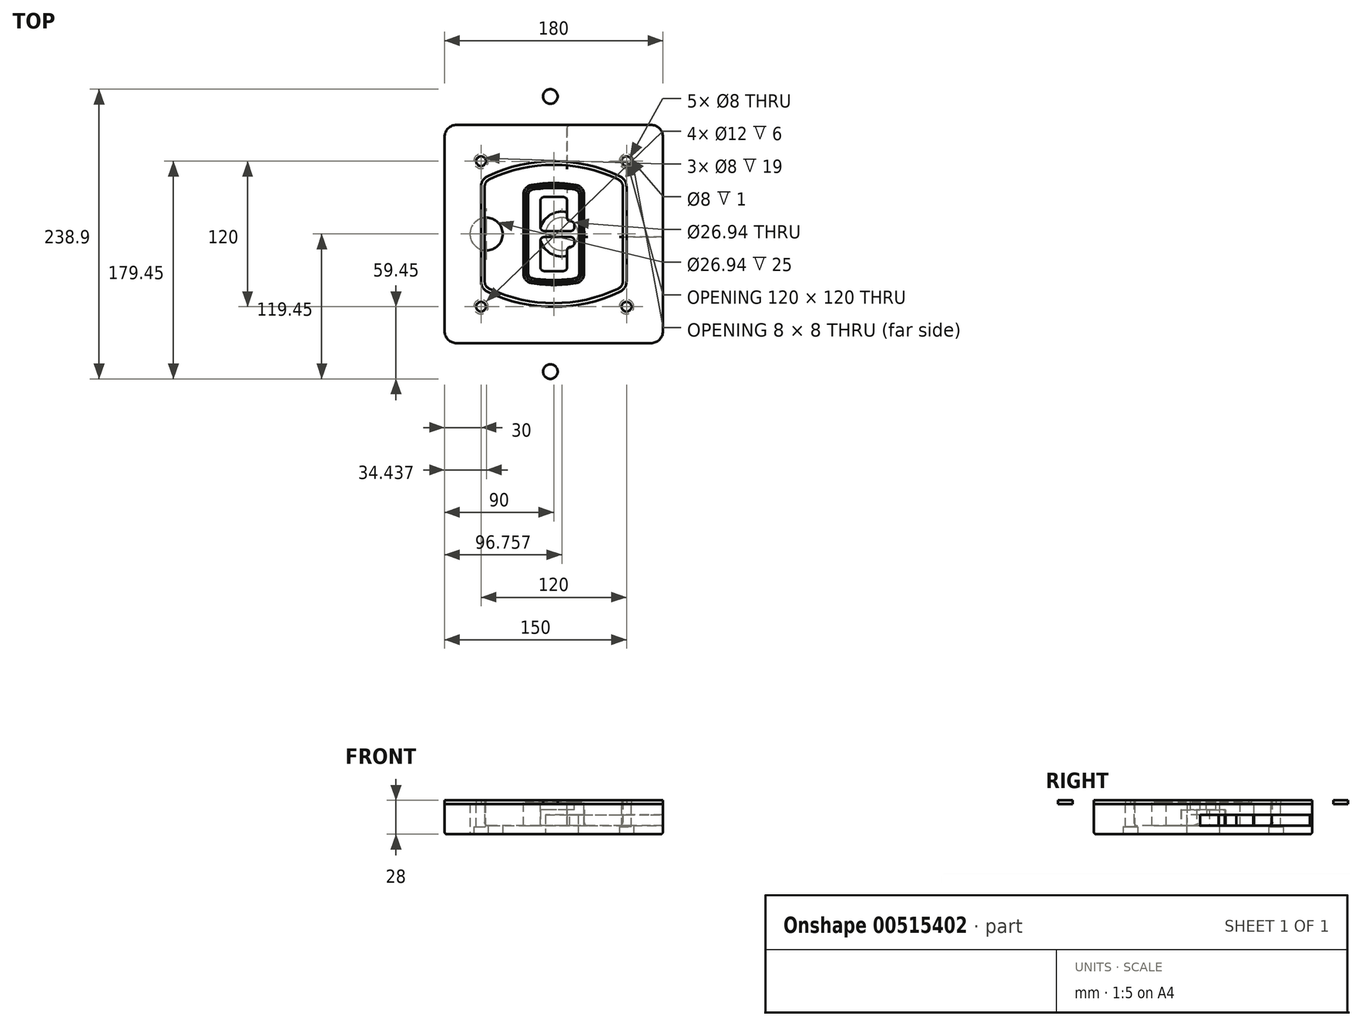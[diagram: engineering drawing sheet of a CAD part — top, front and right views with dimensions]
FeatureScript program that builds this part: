
annotation { "Feature Type Name" : "Feature", "Feature Type Description" : "" }
export const myFeature = defineFeature(function(context is Context, id is Id, definition is map)
    precondition{}
    {
        {
            var Q0;
            Q0=qCreatedBy(makeId("Top.planeOp"),FACE);
            var sketch = newSketch(context, id + "F0", { "sketchPlane" : qUnion([Q0])});
            skPoint(sketch, "E0.rect.middle", {"position": v(0, 0) * mm});
            skLineSegment(sketch, "E1.bottom", {"start": v(-80, -90) * mm, "end": v(80, -90) * mm});
            skLineSegment(sketch, "E1.top", {"start": v(-80, 90) * mm, "end": v(80, 90) * mm});
            skLineSegment(sketch, "E1.left", {"start": v(-90, -80) * mm, "end": v(-90, 80) * mm});
            skLineSegment(sketch, "E1.right", {"start": v(90, -80) * mm, "end": v(90, 80) * mm});
            skLineSegment(sketch, "E2", {"start": v(-90, 90) * mm, "end": v(90, -90) * mm, "construction": true});
            skLineSegment(sketch, "E3", {"start": v(90, 90) * mm, "end": v(-90, -90) * mm, "construction": true});
            skCircle(sketch, "E4", {"center": v(-60, 60) * mm, "radius": 4 * mm});
            skCircle(sketch, "E5", {"center": v(60, 60) * mm, "radius": 4 * mm});
            skCircle(sketch, "E6", {"center": v(60, -60) * mm, "radius": 4 * mm});
            skCircle(sketch, "E7", {"center": v(-60, -60) * mm, "radius": 4 * mm});
            skLineSegment(sketch, "E8", {"start": v(-60, 60) * mm, "end": v(60, 60) * mm, "construction": true});
            skLineSegment(sketch, "E9", {"start": v(60, 60) * mm, "end": v(60, -60) * mm, "construction": true});
            skLineSegment(sketch, "E10", {"start": v(60, -60) * mm, "end": v(-60, -60) * mm, "construction": true});
            skLineSegment(sketch, "E11", {"start": v(-60, -60) * mm, "end": v(-60, 60) * mm, "construction": true});
            skLineSegment(sketch, "E12", {"start": v(-60, 38.83) * mm, "end": v(-60, -38.83) * mm});
            skLineSegment(sketch, "E13", {"start": v(60, 38.83) * mm, "end": v(60, -38.83) * mm});
            skArc(sketch, "E14", {"start": v(54.26, 47.88) * mm, "mid": v(0, 60) * mm, "end": v(-54.26, 47.88) * mm});
            skArc(sketch, "E15", {"start": v(-54.26, -47.88) * mm, "mid": v(0, -60) * mm, "end": v(54.26, -47.88) * mm});
            skLineSegment(sketch, "E16", {"start": v(-60, 0) * mm, "end": v(60, 0) * mm, "construction": true});
            skPoint(sketch, "E17.visualSharp", {"position": v(-60, -45) * mm});
            skArc(sketch, "E17.filletArc", {"start": v(-60, -38.83) * mm, "mid": v(-58.44, -44.2) * mm, "end": v(-54.26, -47.88) * mm});
            skPoint(sketch, "E18.visualSharp", {"position": v(-60, 45) * mm});
            skArc(sketch, "E18.filletArc", {"start": v(-54.26, 47.88) * mm, "mid": v(-58.44, 44.2) * mm, "end": v(-60, 38.83) * mm});
            skPoint(sketch, "E19.visualSharp", {"position": v(60, 45) * mm});
            skArc(sketch, "E19.filletArc", {"start": v(60, 38.83) * mm, "mid": v(58.44, 44.2) * mm, "end": v(54.26, 47.88) * mm});
            skPoint(sketch, "E20.visualSharp", {"position": v(60, -45) * mm});
            skArc(sketch, "E20.filletArc", {"start": v(54.26, -47.88) * mm, "mid": v(58.44, -44.2) * mm, "end": v(60, -38.83) * mm});
            skPoint(sketch, "E21.visualSharp", {"position": v(-90, 90) * mm});
            skArc(sketch, "E21.filletArc", {"start": v(-80, 90) * mm, "mid": v(-87.07, 87.07) * mm, "end": v(-90, 80) * mm});
            skPoint(sketch, "E22.visualSharp", {"position": v(90, 90) * mm});
            skArc(sketch, "E22.filletArc", {"start": v(90, 80) * mm, "mid": v(87.07, 87.07) * mm, "end": v(80, 90) * mm});
            skPoint(sketch, "E23.visualSharp", {"position": v(90, -90) * mm});
            skArc(sketch, "E23.filletArc", {"start": v(80, -90) * mm, "mid": v(87.07, -87.07) * mm, "end": v(90, -80) * mm});
            skPoint(sketch, "E24.visualSharp", {"position": v(-90, -90) * mm});
            skArc(sketch, "E24.filletArc", {"start": v(-90, -80) * mm, "mid": v(-87.07, -87.07) * mm, "end": v(-80, -90) * mm});
            skArc(sketch, "E25.0", {"start": v(57, 38.83) * mm, "mid": v(55.9, 42.58) * mm, "end": v(52.98, 45.17) * mm});
            skLineSegment(sketch, "E25.1", {"start": v(57, 38.83) * mm, "end": v(57, -38.83) * mm});
            skArc(sketch, "E25.2", {"start": v(52.98, -45.17) * mm, "mid": v(55.9, -42.58) * mm, "end": v(57, -38.83) * mm});
            skArc(sketch, "E25.3", {"start": v(-52.98, -45.17) * mm, "mid": v(0, -57) * mm, "end": v(52.98, -45.17) * mm});
            skArc(sketch, "E25.4", {"start": v(-57, -38.83) * mm, "mid": v(-55.9, -42.58) * mm, "end": v(-52.98, -45.17) * mm});
            skArc(sketch, "E25.5", {"start": v(52.98, 45.17) * mm, "mid": v(0, 57) * mm, "end": v(-52.98, 45.17) * mm});
            skLineSegment(sketch, "E25.6", {"start": v(-57, 38.83) * mm, "end": v(-57, -38.83) * mm});
            skArc(sketch, "E25.7", {"start": v(-52.98, 45.17) * mm, "mid": v(-55.9, 42.58) * mm, "end": v(-57, 38.83) * mm});
            skArc(sketch, "E26.0", {"start": v(-55.96, 51.5) * mm, "mid": v(-61.82, 46.33) * mm, "end": v(-64, 38.83) * mm});
            skArc(sketch, "E26.1", {"start": v(55.96, 51.5) * mm, "mid": v(0, 64) * mm, "end": v(-55.96, 51.5) * mm});
            skArc(sketch, "E26.2", {"start": v(64, 38.83) * mm, "mid": v(61.82, 46.33) * mm, "end": v(55.96, 51.5) * mm});
            skLineSegment(sketch, "E26.3", {"start": v(64, 38.83) * mm, "end": v(64, -38.83) * mm});
            skArc(sketch, "E26.4", {"start": v(55.96, -51.5) * mm, "mid": v(61.82, -46.33) * mm, "end": v(64, -38.83) * mm});
            skLineSegment(sketch, "E26.5", {"start": v(-64, 38.83) * mm, "end": v(-64, -38.83) * mm});
            skArc(sketch, "E26.6", {"start": v(-55.96, -51.5) * mm, "mid": v(0, -64) * mm, "end": v(55.96, -51.5) * mm});
            skArc(sketch, "E26.7", {"start": v(-64, -38.83) * mm, "mid": v(-61.82, -46.33) * mm, "end": v(-55.96, -51.5) * mm});
            skSolve(sketch);
        }
        {
            var Q0;
            Q0=makeQuery(id+"F0.imprint","IMPRINT",FACE,{"disambiguationData":[TD([[makeQuery(id+"F0.imprint","IMPRINT",EDGE,{"derivedFrom":sQuery(id+"F0.wireOp",EDGE,"E1.bottom")}),1.0]])]});
            var Q1;
            Q1=makeQuery(id+"F0.imprint","IMPRINT",FACE,{"disambiguationData":[TD([[makeQuery(id+"F0.imprint","IMPRINT",EDGE,{"derivedFrom":sQuery(id+"F0.wireOp",EDGE,"E12")}),1.0]])]});
            var Q2;
            Q2=makeQuery(id+"F0.imprint","IMPRINT",FACE,{"disambiguationData":[TD([[makeQuery(id+"F0.imprint","IMPRINT",EDGE,{"derivedFrom":sQuery(id+"F0.wireOp",EDGE,"E25.0")}),1.0]])]});
            var Q3;
            Q3=makeQuery(id+"F0.imprint","IMPRINT",FACE,{"disambiguationData":[TD([[makeQuery(id+"F0.imprint","IMPRINT",EDGE,{"derivedFrom":sQuery(id+"F0.wireOp",EDGE,"E12")}),-1.0]])]});
            extrude(context, id + "F1", {"entities" : qUnion([Q0, Q1, Q2, Q3]), "oppositeDirection" : true, "depth" : 25 * mm});
        }
        {
            var Q0;
            Q0=makeQuery(id+"F0.imprint","IMPRINT",FACE,{"disambiguationData":[TD([[makeQuery(id+"F0.imprint","IMPRINT",EDGE,{"derivedFrom":sQuery(id+"F0.wireOp",EDGE,"E12")}),1.0]])]});
            extrude(context, id + "F2", {"entities" : qUnion([Q0]), "operationType" : NewBodyOperationType.ADD, "depth" : 3 * mm});
        }
        {
            var Q0;
            Q0=makeQuery(id+"F0.imprint","IMPRINT",FACE,{"disambiguationData":[TD([[makeQuery(id+"F0.imprint","IMPRINT",EDGE,{"derivedFrom":sQuery(id+"F0.wireOp",EDGE,"E25.0")}),1.0]])]});
            extrude(context, id + "F3", {"entities" : qUnion([Q0]), "operationType" : NewBodyOperationType.REMOVE, "oppositeDirection" : true, "depth" : 18 * mm});
        }
        {
            var Q0;
            Q0=makeQuery(id+"F2.opExtrude","CAP_FACE",FACE,{"disambiguationData":[OSD([sQuery(id+"F0.wireOp",EDGE,"E12"),sQuery(id+"F0.wireOp",EDGE,"E13"),sQuery(id+"F0.wireOp",EDGE,"E14"),sQuery(id+"F0.wireOp",EDGE,"E15"),sQuery(id+"F0.wireOp",EDGE,"E17.filletArc"),sQuery(id+"F0.wireOp",EDGE,"E18.filletArc"),sQuery(id+"F0.wireOp",EDGE,"E19.filletArc"),sQuery(id+"F0.wireOp",EDGE,"E20.filletArc"),sQuery(id+"F0.wireOp",EDGE,"E25.0"),sQuery(id+"F0.wireOp",EDGE,"E25.1"),sQuery(id+"F0.wireOp",EDGE,"E25.2"),sQuery(id+"F0.wireOp",EDGE,"E25.3"),sQuery(id+"F0.wireOp",EDGE,"E25.4"),sQuery(id+"F0.wireOp",EDGE,"E25.5"),sQuery(id+"F0.wireOp",EDGE,"E25.6"),sQuery(id+"F0.wireOp",EDGE,"E25.7")])],"isStart":false});
            var sketch = newSketch(context, id + "F4", { "sketchPlane" : qUnion([Q0])});
            skArc(sketch, "E27.0", {"start": v(-18.34, -40.45) * mm, "mid": v(0, -42) * mm, "end": v(18.34, -40.45) * mm});
            skArc(sketch, "E28.0", {"start": v(18.34, 40.45) * mm, "mid": v(0, 42) * mm, "end": v(-18.34, 40.45) * mm});
            skLineSegment(sketch, "E29", {"start": v(-25, 32.57) * mm, "end": v(-25, -32.57) * mm});
            skLineSegment(sketch, "E30", {"start": v(25, 32.57) * mm, "end": v(25, -32.57) * mm});
            skLineSegment(sketch, "E31", {"start": v(-25, 39.1) * mm, "end": v(25, 39.1) * mm, "construction": true});
            skLineSegment(sketch, "E32", {"start": v(-25, -39.1) * mm, "end": v(25, -39.1) * mm, "construction": true});
            skPoint(sketch, "E33.visualSharp", {"position": v(-25, 39.1) * mm});
            skArc(sketch, "E33.filletArc", {"start": v(-18.34, 40.45) * mm, "mid": v(-23.11, 37.73) * mm, "end": v(-25, 32.57) * mm});
            skPoint(sketch, "E34.visualSharp", {"position": v(25, 39.1) * mm});
            skArc(sketch, "E34.filletArc", {"start": v(25, 32.57) * mm, "mid": v(23.11, 37.73) * mm, "end": v(18.34, 40.45) * mm});
            skPoint(sketch, "E35.visualSharp", {"position": v(25, -39.1) * mm});
            skArc(sketch, "E35.filletArc", {"start": v(18.34, -40.45) * mm, "mid": v(23.11, -37.73) * mm, "end": v(25, -32.57) * mm});
            skPoint(sketch, "E36.visualSharp", {"position": v(-25, -39.1) * mm});
            skArc(sketch, "E36.filletArc", {"start": v(-25, -32.57) * mm, "mid": v(-23.11, -37.73) * mm, "end": v(-18.34, -40.45) * mm});
            skArc(sketch, "E37.0", {"start": v(52.98, 45.17) * mm, "mid": v(0, 57) * mm, "end": v(-52.98, 45.17) * mm});
            skArc(sketch, "E37.1", {"start": v(-52.98, 45.17) * mm, "mid": v(-55.9, 42.58) * mm, "end": v(-57, 38.83) * mm});
            skLineSegment(sketch, "E37.2", {"start": v(-57, 38.83) * mm, "end": v(-57, -38.83) * mm});
            skArc(sketch, "E37.3", {"start": v(-57, -38.83) * mm, "mid": v(-55.9, -42.58) * mm, "end": v(-52.98, -45.17) * mm});
            skArc(sketch, "E37.4", {"start": v(-52.98, -45.17) * mm, "mid": v(0, -57) * mm, "end": v(52.98, -45.17) * mm});
            skArc(sketch, "E37.5", {"start": v(52.98, -45.17) * mm, "mid": v(55.9, -42.58) * mm, "end": v(57, -38.83) * mm});
            skLineSegment(sketch, "E37.6", {"start": v(57, 38.83) * mm, "end": v(57, -38.83) * mm});
            skArc(sketch, "E37.7", {"start": v(57, 38.83) * mm, "mid": v(55.9, 42.58) * mm, "end": v(52.98, 45.17) * mm});
            skLineSegment(sketch, "E38.0", {"start": v(23, 32.57) * mm, "end": v(23, -32.57) * mm});
            skArc(sketch, "E38.1", {"start": v(18, -38.48) * mm, "mid": v(21.58, -36.44) * mm, "end": v(23, -32.57) * mm});
            skArc(sketch, "E38.2", {"start": v(-18, -38.48) * mm, "mid": v(0, -40) * mm, "end": v(18, -38.48) * mm});
            skArc(sketch, "E38.3", {"start": v(-23, -32.57) * mm, "mid": v(-21.58, -36.44) * mm, "end": v(-18, -38.48) * mm});
            skLineSegment(sketch, "E38.4", {"start": v(-23, 32.57) * mm, "end": v(-23, -32.57) * mm});
            skArc(sketch, "E38.5", {"start": v(23, 32.57) * mm, "mid": v(21.58, 36.44) * mm, "end": v(18, 38.48) * mm});
            skArc(sketch, "E38.6", {"start": v(-18, 38.48) * mm, "mid": v(-21.58, 36.44) * mm, "end": v(-23, 32.57) * mm});
            skArc(sketch, "E38.7", {"start": v(18, 38.48) * mm, "mid": v(0, 40) * mm, "end": v(-18, 38.48) * mm});
            skArc(sketch, "E39.0", {"start": v(21, 32.57) * mm, "mid": v(20.06, 35.15) * mm, "end": v(17.67, 36.5) * mm});
            skLineSegment(sketch, "E39.1", {"start": v(21, 32.57) * mm, "end": v(21, -32.57) * mm});
            skArc(sketch, "E39.2", {"start": v(17.67, -36.5) * mm, "mid": v(20.06, -35.15) * mm, "end": v(21, -32.57) * mm});
            skArc(sketch, "E39.3", {"start": v(-17.67, -36.5) * mm, "mid": v(0, -38) * mm, "end": v(17.67, -36.5) * mm});
            skArc(sketch, "E39.4", {"start": v(-21, -32.57) * mm, "mid": v(-20.06, -35.15) * mm, "end": v(-17.67, -36.5) * mm});
            skArc(sketch, "E39.5", {"start": v(17.67, 36.5) * mm, "mid": v(0, 38) * mm, "end": v(-17.67, 36.5) * mm});
            skLineSegment(sketch, "E39.6", {"start": v(-21, 32.57) * mm, "end": v(-21, -32.57) * mm});
            skArc(sketch, "E39.7", {"start": v(-17.67, 36.5) * mm, "mid": v(-20.06, 35.15) * mm, "end": v(-21, 32.57) * mm});
            skLineSegment(sketch, "E40", {"start": v(-25, 0) * mm, "end": v(25, 0) * mm, "construction": true});
            skLineSegment(sketch, "E41", {"start": v(-11, 5.5) * mm, "end": v(-11, 27.5) * mm});
            skLineSegment(sketch, "E42", {"start": v(-8, 30.5) * mm, "end": v(8, 30.5) * mm});
            skLineSegment(sketch, "E43", {"start": v(11, 27.5) * mm, "end": v(11, 13.5) * mm});
            skLineSegment(sketch, "E44", {"start": v(14, 10.5) * mm, "end": v(14, 10.5) * mm});
            skLineSegment(sketch, "E45", {"start": v(17, 7.5) * mm, "end": v(17, 5.5) * mm});
            skLineSegment(sketch, "E46", {"start": v(14, 2.5) * mm, "end": v(-8, 2.5) * mm});
            skPoint(sketch, "E47.visualSharp", {"position": v(-11, 30.5) * mm});
            skArc(sketch, "E47.filletArc", {"start": v(-8, 30.5) * mm, "mid": v(-10.12, 29.62) * mm, "end": v(-11, 27.5) * mm});
            skPoint(sketch, "E48.visualSharp", {"position": v(11, 30.5) * mm});
            skArc(sketch, "E48.filletArc", {"start": v(11, 27.5) * mm, "mid": v(10.12, 29.62) * mm, "end": v(8, 30.5) * mm});
            skPoint(sketch, "E49.visualSharp", {"position": v(11, 10.5) * mm});
            skArc(sketch, "E49.filletArc", {"start": v(11, 13.5) * mm, "mid": v(11.88, 11.38) * mm, "end": v(14, 10.5) * mm});
            skPoint(sketch, "E50.visualSharp", {"position": v(17, 10.5) * mm});
            skArc(sketch, "E50.filletArc", {"start": v(17, 7.5) * mm, "mid": v(16.12, 9.62) * mm, "end": v(14, 10.5) * mm});
            skPoint(sketch, "E51.visualSharp", {"position": v(17, 2.5) * mm});
            skArc(sketch, "E51.filletArc", {"start": v(14, 2.5) * mm, "mid": v(16.12, 3.38) * mm, "end": v(17, 5.5) * mm});
            skPoint(sketch, "E52.visualSharp", {"position": v(-11, 2.5) * mm});
            skArc(sketch, "E52.filletArc", {"start": v(-11, 5.5) * mm, "mid": v(-10.12, 3.38) * mm, "end": v(-8, 2.5) * mm});
            skLineSegment(sketch, "E53.0.MirrorCS", {"start": v(14, -2.5) * mm, "end": v(-8, -2.5) * mm});
            skArc(sketch, "E54.0.MirrorCS", {"start": v(-11, -5.5) * mm, "mid": v(-10.12, -3.38) * mm, "end": v(-8, -2.5) * mm});
            skLineSegment(sketch, "E55.0.MirrorCS", {"start": v(-11, -5.5) * mm, "end": v(-11, -27.5) * mm});
            skArc(sketch, "E56.0.MirrorCS", {"start": v(-8, -30.5) * mm, "mid": v(-10.12, -29.62) * mm, "end": v(-11, -27.5) * mm});
            skLineSegment(sketch, "E57.0.MirrorCS", {"start": v(-8, -30.5) * mm, "end": v(8, -30.5) * mm});
            skArc(sketch, "E58.0.MirrorCS", {"start": v(11, -27.5) * mm, "mid": v(10.12, -29.62) * mm, "end": v(8, -30.5) * mm});
            skLineSegment(sketch, "E59.0.MirrorCS", {"start": v(11, -27.5) * mm, "end": v(11, -13.5) * mm});
            skArc(sketch, "E60.0.MirrorCS", {"start": v(11, -13.5) * mm, "mid": v(11.88, -11.38) * mm, "end": v(14, -10.5) * mm});
            skArc(sketch, "E61.0.MirrorCS", {"start": v(17, -7.5) * mm, "mid": v(16.12, -9.62) * mm, "end": v(14, -10.5) * mm});
            skLineSegment(sketch, "E62.0.MirrorCS", {"start": v(17, -7.5) * mm, "end": v(17, -5.5) * mm});
            skArc(sketch, "E63.0.MirrorCS", {"start": v(14, -2.5) * mm, "mid": v(16.12, -3.38) * mm, "end": v(17, -5.5) * mm});
            skSolve(sketch);
        }
        {
            var Q0;
            Q0=makeQuery(id+"F4.imprint","IMPRINT",FACE,{"disambiguationData":[TD([[makeQuery(id+"F4.imprint","IMPRINT",EDGE,{"derivedFrom":sQuery(id+"F4.wireOp",EDGE,"E27.0")}),1.0]])]});
            var Q1;
            Q1=makeQuery(id+"F4.imprint","IMPRINT",FACE,{"disambiguationData":[TD([[makeQuery(id+"F4.imprint","IMPRINT",EDGE,{"derivedFrom":sQuery(id+"F4.wireOp",EDGE,"E38.0")}),-1.0]])]});
            var Q2;
            Q2=makeQuery(id+"F4.imprint","IMPRINT",FACE,{"disambiguationData":[TD([[makeQuery(id+"F4.imprint","IMPRINT",EDGE,{"derivedFrom":sQuery(id+"F4.wireOp",EDGE,"E39.0")}),1.0]])]});
            extrude(context, id + "F5", {"entities" : qUnion([Q0, Q1, Q2]), "operationType" : NewBodyOperationType.ADD, "endBound" : BoundingType.UP_TO_NEXT, "oppositeDirection" : true, "depth" : 25 * mm});
        }
        {
            var Q0;
            Q0=makeQuery(id+"F4.imprint","IMPRINT",FACE,{"disambiguationData":[TD([[makeQuery(id+"F4.imprint","IMPRINT",EDGE,{"derivedFrom":sQuery(id+"F4.wireOp",EDGE,"E38.0")}),-1.0]])]});
            extrude(context, id + "F6", {"entities" : qUnion([Q0]), "operationType" : NewBodyOperationType.REMOVE, "oppositeDirection" : true, "depth" : 2 * mm});
        }
        {
            var Q0;
            Q0=makeQuery(id+"F1.opExtrude","CAP_FACE",FACE,{"disambiguationData":[OSD([sQuery(id+"F0.wireOp",EDGE,"E1.bottom"),sQuery(id+"F0.wireOp",EDGE,"E1.top"),sQuery(id+"F0.wireOp",EDGE,"E1.left"),sQuery(id+"F0.wireOp",EDGE,"E1.right"),sQuery(id+"F0.wireOp",EDGE,"E4"),sQuery(id+"F0.wireOp",EDGE,"E5"),sQuery(id+"F0.wireOp",EDGE,"E6"),sQuery(id+"F0.wireOp",EDGE,"E7"),sQuery(id+"F0.wireOp",EDGE,"E21.filletArc"),sQuery(id+"F0.wireOp",EDGE,"E22.filletArc"),sQuery(id+"F0.wireOp",EDGE,"E23.filletArc"),sQuery(id+"F0.wireOp",EDGE,"E24.filletArc")])],"isStart":false});
            var sketch = newSketch(context, id + "F7", { "sketchPlane" : qUnion([Q0])});
            skCircle(sketch, "E64", {"center": v(6.76, 0) * mm, "radius": 13.47 * mm});
            skCircle(sketch, "E65", {"center": v(-55.56, 0) * mm, "radius": 13.47 * mm});
            skLineSegment(sketch, "E66", {"start": v(90, 0) * mm, "end": v(-90, 0) * mm});
            skCircle(sketch, "E67", {"center": v(6.76, 0) * mm, "radius": 18.47 * mm});
            skCircle(sketch, "E68", {"center": v(60, -60) * mm, "radius": 6 * mm});
            skCircle(sketch, "E69", {"center": v(-60, -60) * mm, "radius": 6 * mm});
            skCircle(sketch, "E70", {"center": v(-60, 60) * mm, "radius": 6 * mm});
            skCircle(sketch, "E71", {"center": v(60, 60) * mm, "radius": 6 * mm});
            skSolve(sketch);
        }
        {
            var Q0;
            {var subQ1=sQuery(id+"F7.wireOp",EDGE,"E66");var subQ4=sQuery(id+"F7.wireOp",EDGE,"E64");var subQ6=makeQuery(id+"F7.imprint","INTERSECT",VERTEX,{"disambiguationData":[OD(0.0)],"derivedFrom":[subQ4,subQ1]});Q0=makeQuery(id+"F7.imprint","IMPRINT",FACE,{"disambiguationData":[TD([[makeQuery(id+"F7.imprint","IMPRINT",EDGE,{"disambiguationData":[TD([[subQ6,-1.0]])],"derivedFrom":subQ4}),-1.0]])]});}
            var Q1;
            {var subQ0=sQuery(id+"F7.wireOp",EDGE,"E66");var subQ1=sQuery(id+"F7.wireOp",EDGE,"E64");var subQ3=makeQuery(id+"F7.imprint","INTERSECT",VERTEX,{"disambiguationData":[OD(0.0)],"derivedFrom":[subQ1,subQ0]});Q1=makeQuery(id+"F7.imprint","IMPRINT",FACE,{"disambiguationData":[TD([[makeQuery(id+"F7.imprint","IMPRINT",EDGE,{"disambiguationData":[TD([[subQ3,-1.0]])],"derivedFrom":subQ1}),1.0]])]});}
            var Q2;
            {var subQ0=sQuery(id+"F7.wireOp",EDGE,"E66");var subQ1=sQuery(id+"F7.wireOp",EDGE,"E64");var subQ3=makeQuery(id+"F7.imprint","INTERSECT",VERTEX,{"disambiguationData":[OD(0.0)],"derivedFrom":[subQ1,subQ0]});Q2=makeQuery(id+"F7.imprint","IMPRINT",FACE,{"disambiguationData":[TD([[makeQuery(id+"F7.imprint","IMPRINT",EDGE,{"disambiguationData":[TD([[subQ3,1.0]])],"derivedFrom":subQ1}),1.0]])]});}
            var Q3;
            {var subQ1=sQuery(id+"F7.wireOp",EDGE,"E66");var subQ4=sQuery(id+"F7.wireOp",EDGE,"E64");var subQ6=makeQuery(id+"F7.imprint","INTERSECT",VERTEX,{"disambiguationData":[OD(0.0)],"derivedFrom":[subQ4,subQ1]});Q3=makeQuery(id+"F7.imprint","IMPRINT",FACE,{"disambiguationData":[TD([[makeQuery(id+"F7.imprint","IMPRINT",EDGE,{"disambiguationData":[TD([[subQ6,1.0]])],"derivedFrom":subQ4}),-1.0]])]});}
            extrude(context, id + "F8", {"entities" : qUnion([Q0, Q1, Q2, Q3]), "operationType" : NewBodyOperationType.ADD, "oppositeDirection" : true, "depth" : 20 * mm});
        }
        {
            var Q0;
            {var subQ0=sQuery(id+"F7.wireOp",EDGE,"E66");var subQ1=sQuery(id+"F7.wireOp",EDGE,"E64");var subQ3=makeQuery(id+"F7.imprint","INTERSECT",VERTEX,{"disambiguationData":[OD(0.0)],"derivedFrom":[subQ1,subQ0]});Q0=makeQuery(id+"F7.imprint","IMPRINT",FACE,{"disambiguationData":[TD([[makeQuery(id+"F7.imprint","IMPRINT",EDGE,{"disambiguationData":[TD([[subQ3,-1.0]])],"derivedFrom":subQ1}),1.0]])]});}
            var Q1;
            {var subQ0=sQuery(id+"F7.wireOp",EDGE,"E66");var subQ1=sQuery(id+"F7.wireOp",EDGE,"E64");var subQ3=makeQuery(id+"F7.imprint","INTERSECT",VERTEX,{"disambiguationData":[OD(0.0)],"derivedFrom":[subQ1,subQ0]});Q1=makeQuery(id+"F7.imprint","IMPRINT",FACE,{"disambiguationData":[TD([[makeQuery(id+"F7.imprint","IMPRINT",EDGE,{"disambiguationData":[TD([[subQ3,1.0]])],"derivedFrom":subQ1}),1.0]])]});}
            extrude(context, id + "F9", {"entities" : qUnion([Q0, Q1]), "operationType" : NewBodyOperationType.REMOVE, "oppositeDirection" : true, "depth" : 16 * mm});
        }
        {
            var Q0;
            {var subQ0=sQuery(id+"F7.wireOp",EDGE,"E66");var subQ1=sQuery(id+"F7.wireOp",EDGE,"E65");var subQ3=makeQuery(id+"F7.imprint","INTERSECT",VERTEX,{"disambiguationData":[OD(0.0)],"derivedFrom":[subQ1,subQ0]});Q0=makeQuery(id+"F7.imprint","IMPRINT",FACE,{"disambiguationData":[TD([[makeQuery(id+"F7.imprint","IMPRINT",EDGE,{"disambiguationData":[TD([[subQ3,-1.0]])],"derivedFrom":subQ1}),1.0]])]});}
            var Q1;
            {var subQ0=sQuery(id+"F7.wireOp",EDGE,"E66");var subQ1=sQuery(id+"F7.wireOp",EDGE,"E65");var subQ3=makeQuery(id+"F7.imprint","INTERSECT",VERTEX,{"disambiguationData":[OD(0.0)],"derivedFrom":[subQ1,subQ0]});Q1=makeQuery(id+"F7.imprint","IMPRINT",FACE,{"disambiguationData":[TD([[makeQuery(id+"F7.imprint","IMPRINT",EDGE,{"disambiguationData":[TD([[subQ3,1.0]])],"derivedFrom":subQ1}),1.0]])]});}
            extrude(context, id + "F10", {"entities" : qUnion([Q0, Q1]), "operationType" : NewBodyOperationType.REMOVE, "oppositeDirection" : true, "depth" : 25 * mm});
        }
        {
            var Q0;
            Q0=makeQuery(id+"F7.imprint","IMPRINT",FACE,{"disambiguationData":[TD([[makeQuery(id+"F7.imprint","IMPRINT",EDGE,{"derivedFrom":sQuery(id+"F7.wireOp",EDGE,"E68")}),1.0]])]});
            var Q1;
            Q1=makeQuery(id+"F7.imprint","IMPRINT",FACE,{"disambiguationData":[TD([[makeQuery(id+"F7.imprint","IMPRINT",EDGE,{"derivedFrom":makeQuery(id+"F1.opExtrude","CAP_EDGE",EDGE,{"disambiguationData":[OSD([sQuery(id+"F0.wireOp",EDGE,"E5")])],"isStart":false})}),-1.0]])]});
            var Q2;
            Q2=makeQuery(id+"F7.imprint","IMPRINT",FACE,{"disambiguationData":[TD([[makeQuery(id+"F7.imprint","IMPRINT",EDGE,{"derivedFrom":sQuery(id+"F7.wireOp",EDGE,"E69")}),1.0]])]});
            var Q3;
            Q3=makeQuery(id+"F7.imprint","IMPRINT",FACE,{"disambiguationData":[TD([[makeQuery(id+"F7.imprint","IMPRINT",EDGE,{"derivedFrom":makeQuery(id+"F1.opExtrude","CAP_EDGE",EDGE,{"disambiguationData":[OSD([sQuery(id+"F0.wireOp",EDGE,"E4")])],"isStart":false})}),-1.0]])]});
            var Q4;
            Q4=makeQuery(id+"F7.imprint","IMPRINT",FACE,{"disambiguationData":[TD([[makeQuery(id+"F7.imprint","IMPRINT",EDGE,{"derivedFrom":sQuery(id+"F7.wireOp",EDGE,"E70")}),1.0]])]});
            var Q5;
            Q5=makeQuery(id+"F7.imprint","IMPRINT",FACE,{"disambiguationData":[TD([[makeQuery(id+"F7.imprint","IMPRINT",EDGE,{"derivedFrom":makeQuery(id+"F1.opExtrude","CAP_EDGE",EDGE,{"disambiguationData":[OSD([sQuery(id+"F0.wireOp",EDGE,"E7")])],"isStart":false})}),-1.0]])]});
            var Q6;
            Q6=makeQuery(id+"F7.imprint","IMPRINT",FACE,{"disambiguationData":[TD([[makeQuery(id+"F7.imprint","IMPRINT",EDGE,{"derivedFrom":sQuery(id+"F7.wireOp",EDGE,"E71")}),1.0]])]});
            var Q7;
            Q7=makeQuery(id+"F7.imprint","IMPRINT",FACE,{"disambiguationData":[TD([[makeQuery(id+"F7.imprint","IMPRINT",EDGE,{"derivedFrom":makeQuery(id+"F1.opExtrude","CAP_EDGE",EDGE,{"disambiguationData":[OSD([sQuery(id+"F0.wireOp",EDGE,"E6")])],"isStart":false})}),-1.0]])]});
            extrude(context, id + "F11", {"entities" : qUnion([Q0, Q1, Q2, Q3, Q4, Q5, Q6, Q7]), "operationType" : NewBodyOperationType.REMOVE, "oppositeDirection" : true, "depth" : 6 * mm});
        }
        {
            var Q0;
            Q0=makeQuery(id+"F9.boolean.opBoolean","COPY",FACE,{"derivedFrom":makeQuery(id+"F9.opExtrude","CAP_FACE",FACE,{"disambiguationData":[OSD([sQuery(id+"F7.wireOp",EDGE,"E64")])],"isStart":false})});
            var sketch = newSketch(context, id + "F12", { "sketchPlane" : qUnion([Q0])});
            skArc(sketch, "E72.0", {"start": v(11, -88.19) * mm, "mid": v(97.1, -83.6) * mm, "end": v(92.5, 2.5) * mm});
            skLineSegment(sketch, "E72.1", {"start": v(11, -17.97) * mm, "end": v(11, -17.97) * mm});
            skLineSegment(sketch, "E73", {"start": v(92.5, -105.13) * mm, "end": v(102.3, -105.13) * mm});
            skLineSegment(sketch, "E74.0", {"start": v(92.5, 2.5) * mm, "end": v(14, 2.5) * mm});
            skArc(sketch, "E74.1", {"start": v(14, 2.5) * mm, "mid": v(16.12, 3.38) * mm, "end": v(17, 5.5) * mm});
            skLineSegment(sketch, "E74.2", {"start": v(17, 7.5) * mm, "end": v(17, 5.5) * mm});
            skArc(sketch, "E74.3", {"start": v(17, 7.5) * mm, "mid": v(16.12, 9.62) * mm, "end": v(14, 10.5) * mm});
            skArc(sketch, "E74.4", {"start": v(11, 13.5) * mm, "mid": v(11.88, 11.38) * mm, "end": v(14, 10.5) * mm});
            skLineSegment(sketch, "E74.5", {"start": v(11, 13.5) * mm, "end": v(11, -88.19) * mm});
            skLineSegment(sketch, "E74.7", {"start": v(92.5, -2.5) * mm, "end": v(14, -2.5) * mm});
            skArc(sketch, "E74.8", {"start": v(14, -2.5) * mm, "mid": v(16.12, -3.38) * mm, "end": v(17, -5.5) * mm});
            skLineSegment(sketch, "E74.9", {"start": v(17, -7.5) * mm, "end": v(17, -5.5) * mm});
            skArc(sketch, "E74.10", {"start": v(17, -7.5) * mm, "mid": v(16.12, -9.62) * mm, "end": v(14, -10.5) * mm});
            skArc(sketch, "E74.11", {"start": v(11, -13.5) * mm, "mid": v(11.88, -11.38) * mm, "end": v(14, -10.5) * mm});
            skLineSegment(sketch, "E74.12", {"start": v(11, -17.97) * mm, "end": v(11, -13.5) * mm});
            skPoint(sketch, "E75.orphan", {"position": v(11, -27.5) * mm});
            skPoint(sketch, "E76.orphan", {"position": v(-8, -2.5) * mm});
            skPoint(sketch, "E77.orphan", {"position": v(-8, 2.5) * mm});
            skPoint(sketch, "E78.orphan", {"position": v(11, 27.5) * mm});
            skSolve(sketch);
        }
        {
            var Q0;
            {var subQ7=sQuery(id+"F12.wireOp",EDGE,"E72.0");var subQ14=sQuery(id+"F12.wireOp",EDGE,"E72.1");var subQ16=sQuery(id+"F12.wireOp",EDGE,"E74.1");var subQ18=sQuery(id+"F12.wireOp",EDGE,"E74.8");Q0=qUnion([makeQuery(id+"F12.imprint","IMPRINT",FACE,{"disambiguationData":[TD([[makeQuery(id+"F12.imprint","IMPRINT",EDGE,{"derivedFrom":subQ7}),1.0]])]}),makeQuery(id+"F12.imprint","IMPRINT",FACE,{"disambiguationData":[TD([[makeQuery(id+"F12.imprint","IMPRINT",EDGE,{"derivedFrom":subQ14}),1.0]])]}),makeQuery(id+"F12.imprint","IMPRINT",FACE,{"disambiguationData":[TD([[makeQuery(id+"F12.imprint","IMPRINT",EDGE,{"derivedFrom":subQ16}),1.0]])]}),makeQuery(id+"F12.imprint","IMPRINT",FACE,{"disambiguationData":[TD([[makeQuery(id+"F12.imprint","IMPRINT",EDGE,{"derivedFrom":subQ18}),-1.0]])]})]);}
            var Q1;
            Q1=makeQuery(id+"F5.boolean.opBoolean","SPLIT",FACE,{"disambiguationData":[TD([makeQuery(id+"F5.opExtrude","SWEPT_FACE",FACE,{"disambiguationData":[OSD([sQuery(id+"F4.wireOp",EDGE,"E41")])]})])],"derivedFrom":makeQuery(id+"F3.boolean.opBoolean","COPY",FACE,{"derivedFrom":makeQuery(id+"F3.opExtrude","CAP_FACE",FACE,{"disambiguationData":[OSD([sQuery(id+"F0.wireOp",EDGE,"E25.0"),sQuery(id+"F0.wireOp",EDGE,"E25.1"),sQuery(id+"F0.wireOp",EDGE,"E25.2"),sQuery(id+"F0.wireOp",EDGE,"E25.3"),sQuery(id+"F0.wireOp",EDGE,"E25.4"),sQuery(id+"F0.wireOp",EDGE,"E25.5"),sQuery(id+"F0.wireOp",EDGE,"E25.6"),sQuery(id+"F0.wireOp",EDGE,"E25.7")])],"isStart":false})})});
            extrude(context, id + "F13", {"entities" : qUnion([Q0]), "operationType" : NewBodyOperationType.REMOVE, "endBound" : BoundingType.UP_TO_SURFACE, "endBoundEntityFace" : qUnion([Q1]), "depth" : 25 * mm});
        }
        {
            var Q0;
            Q0=makeQuery(id+"F3.boolean.opBoolean","COPY",EDGE,{"derivedFrom":makeQuery(id+"F3.opExtrude","CAP_EDGE",EDGE,{"disambiguationData":[OSD([sQuery(id+"F0.wireOp",EDGE,"E25.6")])],"isStart":false})});
            var Q1;
            Q1=makeQuery(id+"F8.boolean.opBoolean","INTERSECT",EDGE,{"derivedFrom":[makeQuery(id+"F5.opExtrude","SWEPT_FACE",FACE,{"disambiguationData":[OSD([sQuery(id+"F4.wireOp",EDGE,"E30")])]}),makeQuery(id+"F8.opExtrude","CAP_FACE",FACE,{"disambiguationData":[OSD([sQuery(id+"F7.wireOp",EDGE,"E67")])],"isStart":false})]});
            var Q2;
            Q2=makeQuery(id+"F8.boolean.opBoolean","INTERSECT",EDGE,{"disambiguationData":[OD(1.0)],"derivedFrom":[makeQuery(id+"F5.opExtrude","SWEPT_FACE",FACE,{"disambiguationData":[OSD([sQuery(id+"F4.wireOp",EDGE,"E30")])]}),makeQuery(id+"F8.opExtrude","SWEPT_FACE",FACE,{"disambiguationData":[OSD([sQuery(id+"F7.wireOp",EDGE,"E67")])]})]});
            var Q3;
            {var subQ0=makeQuery(id+"F3.boolean.opBoolean","COPY",FACE,{"derivedFrom":makeQuery(id+"F3.opExtrude","CAP_FACE",FACE,{"disambiguationData":[OSD([sQuery(id+"F0.wireOp",EDGE,"E25.0"),sQuery(id+"F0.wireOp",EDGE,"E25.1"),sQuery(id+"F0.wireOp",EDGE,"E25.2"),sQuery(id+"F0.wireOp",EDGE,"E25.3"),sQuery(id+"F0.wireOp",EDGE,"E25.4"),sQuery(id+"F0.wireOp",EDGE,"E25.5"),sQuery(id+"F0.wireOp",EDGE,"E25.6"),sQuery(id+"F0.wireOp",EDGE,"E25.7")])],"isStart":false})});var subQ1=sQuery(id+"F4.wireOp",EDGE,"E30");Q3=makeQuery(id+"F8.boolean.opBoolean","SPLIT",EDGE,{"disambiguationData":[TD([makeQuery(id+"F5.opExtrude","SWEPT_FACE",FACE,{"disambiguationData":[OSD([sQuery(id+"F4.wireOp",EDGE,"E35.filletArc")])]})])],"derivedFrom":makeQuery(id+"F5.opExtrude","TWEAK_EDGE",EDGE,{"derivedFrom":[subQ0,makeQuery(id+"F4.imprint","IMPRINT",EDGE,{"derivedFrom":subQ1})]})});}
            var Q4;
            {var subQ0=sQuery(id+"F0.wireOp",EDGE,"E25.0");var subQ1=sQuery(id+"F0.wireOp",EDGE,"E25.1");var subQ2=sQuery(id+"F0.wireOp",EDGE,"E25.2");var subQ3=sQuery(id+"F0.wireOp",EDGE,"E25.3");var subQ4=sQuery(id+"F0.wireOp",EDGE,"E25.4");var subQ5=sQuery(id+"F0.wireOp",EDGE,"E25.5");var subQ6=sQuery(id+"F0.wireOp",EDGE,"E25.6");var subQ7=sQuery(id+"F0.wireOp",EDGE,"E25.7");Q4=makeQuery(id+"F8.boolean.opBoolean","INTERSECT",EDGE,{"derivedFrom":[makeQuery(id+"F5.boolean.opBoolean","SPLIT",FACE,{"disambiguationData":[TD([makeQuery(id+"F2.opExtrude","SWEPT_FACE",FACE,{"disambiguationData":[OSD([subQ0])]})])],"derivedFrom":makeQuery(id+"F3.boolean.opBoolean","COPY",FACE,{"derivedFrom":makeQuery(id+"F3.opExtrude","CAP_FACE",FACE,{"disambiguationData":[OSD([subQ0,subQ1,subQ2,subQ3,subQ4,subQ5,subQ6,subQ7])],"isStart":false})})}),makeQuery(id+"F8.opExtrude","SWEPT_FACE",FACE,{"disambiguationData":[OSD([sQuery(id+"F7.wireOp",EDGE,"E67")])]})]});}
            var Q5;
            Q5=makeQuery(id+"F8.boolean.opBoolean","INTERSECT",EDGE,{"disambiguationData":[OD(0.0)],"derivedFrom":[makeQuery(id+"F5.opExtrude","SWEPT_FACE",FACE,{"disambiguationData":[OSD([sQuery(id+"F4.wireOp",EDGE,"E30")])]}),makeQuery(id+"F8.opExtrude","SWEPT_FACE",FACE,{"disambiguationData":[OSD([sQuery(id+"F7.wireOp",EDGE,"E67")])]})]});
            fillet(context, id + "F14", {"entities" : qUnion([Q0, Q1, Q2, Q3, Q4, Q5]), "radius" : 3 * mm, "tangentPropagation" : true, "allowEdgeOverflow" : false});
        }
        {
            var Q0;
            Q0=makeQuery(id+"F1.opExtrude","CAP_EDGE",EDGE,{"disambiguationData":[OSD([sQuery(id+"F0.wireOp",EDGE,"E1.bottom")])],"isStart":false});
            fillet(context, id + "F15", {"entities" : qUnion([Q0]), "radius" : 2 * mm, "tangentPropagation" : true, "allowEdgeOverflow" : false});
        }
        {
            var Q0;
            {var subQ0=sQuery(id+"F0.wireOp",EDGE,"E21.filletArc");var subQ1=sQuery(id+"F0.wireOp",EDGE,"E7");var subQ2=sQuery(id+"F0.wireOp",EDGE,"E6");var subQ3=sQuery(id+"F0.wireOp",EDGE,"E5");var subQ4=sQuery(id+"F0.wireOp",EDGE,"E4");var subQ5=sQuery(id+"F0.wireOp",EDGE,"E22.filletArc");var subQ6=sQuery(id+"F0.wireOp",EDGE,"E1.bottom");var subQ7=sQuery(id+"F0.wireOp",EDGE,"E1.right");var subQ8=sQuery(id+"F0.wireOp",EDGE,"E1.top");var subQ9=sQuery(id+"F0.wireOp",EDGE,"E1.left");var subQ10=sQuery(id+"F0.wireOp",EDGE,"E23.filletArc");var subQ11=sQuery(id+"F0.wireOp",EDGE,"E24.filletArc");Q0=makeQuery(id+"F2.boolean.opBoolean","SPLIT",FACE,{"disambiguationData":[TD([makeQuery(id+"F1.opExtrude","SWEPT_FACE",FACE,{"disambiguationData":[OSD([subQ6])]})])],"derivedFrom":makeQuery(id+"F1.opExtrude","CAP_FACE",FACE,{"disambiguationData":[OSD([subQ6,subQ8,subQ9,subQ7,subQ4,subQ3,subQ2,subQ1,subQ0,subQ5,subQ10,subQ11])],"isStart":true})});}
            var sketch = newSketch(context, id + "F16", { "sketchPlane" : qUnion([Q0])});
            skArc(sketch, "E79.0", {"start": v(-80, 90) * mm, "mid": v(-87.07, 87.07) * mm, "end": v(-90, 80) * mm});
            skLineSegment(sketch, "E79.1", {"start": v(-80, 90) * mm, "end": v(80, 90) * mm});
            skArc(sketch, "E79.2", {"start": v(90, 80) * mm, "mid": v(87.07, 87.07) * mm, "end": v(80, 90) * mm});
            skLineSegment(sketch, "E79.3", {"start": v(90, -80) * mm, "end": v(90, 80) * mm});
            skArc(sketch, "E79.4", {"start": v(80, -90) * mm, "mid": v(87.07, -87.07) * mm, "end": v(90, -80) * mm});
            skLineSegment(sketch, "E79.5", {"start": v(-80, -90) * mm, "end": v(80, -90) * mm});
            skArc(sketch, "E79.6", {"start": v(-90, -80) * mm, "mid": v(-87.07, -87.07) * mm, "end": v(-80, -90) * mm});
            skCircle(sketch, "E79.7", {"center": v(-60, -60) * mm, "radius": 4 * mm});
            skCircle(sketch, "E79.8", {"center": v(60, -60) * mm, "radius": 4 * mm});
            skCircle(sketch, "E79.9", {"center": v(60, 60) * mm, "radius": 4 * mm});
            skCircle(sketch, "E79.10", {"center": v(-60, 60) * mm, "radius": 4 * mm});
            skLineSegment(sketch, "E79.11", {"start": v(-60, 38.83) * mm, "end": v(-60, -38.83) * mm});
            skArc(sketch, "E79.12", {"start": v(-54.26, 47.88) * mm, "mid": v(-58.44, 44.2) * mm, "end": v(-60, 38.83) * mm});
            skArc(sketch, "E79.13", {"start": v(54.26, 47.88) * mm, "mid": v(0, 60) * mm, "end": v(-54.26, 47.88) * mm});
            skArc(sketch, "E79.14", {"start": v(60, 38.83) * mm, "mid": v(58.44, 44.2) * mm, "end": v(54.26, 47.88) * mm});
            skLineSegment(sketch, "E79.15", {"start": v(60, 38.83) * mm, "end": v(60, -38.83) * mm});
            skArc(sketch, "E79.16", {"start": v(54.26, -47.88) * mm, "mid": v(58.44, -44.2) * mm, "end": v(60, -38.83) * mm});
            skArc(sketch, "E79.17", {"start": v(-54.26, -47.88) * mm, "mid": v(0, -60) * mm, "end": v(54.26, -47.88) * mm});
            skArc(sketch, "E79.18", {"start": v(-60, -38.83) * mm, "mid": v(-58.44, -44.2) * mm, "end": v(-54.26, -47.88) * mm});
            skLineSegment(sketch, "E79.19", {"start": v(-90, -80) * mm, "end": v(-90, 80) * mm});
            skSolve(sketch);
        }
        {
            var Q0;
            Q0=qCreatedBy(makeId("Top.planeOp"),FACE);
            var sketch = newSketch(context, id + "F17", { "sketchPlane" : qUnion([Q0])});
            skLineSegment(sketch, "E80", {"start": v(-16.69, 108) * mm, "end": v(-16.69, 119) * mm});
            skLineSegment(sketch, "E81", {"start": v(11.19, 119) * mm, "end": v(11.19, 108) * mm});
            skLineSegment(sketch, "E82", {"start": v(11.19, 108) * mm, "end": v(28.9, 90.3) * mm});
            skArc(sketch, "E83", {"start": v(11.19, 119) * mm, "mid": v(-2.75, 128.45) * mm, "end": v(-16.69, 119) * mm});
            skLineSegment(sketch, "E84", {"start": v(-16.69, 108) * mm, "end": v(-30.3, 90.3) * mm});
            skCircle(sketch, "E85", {"center": v(-2.75, 113.45) * mm, "radius": 6 * mm});
            skLineSegment(sketch, "E86", {"start": v(-2.75, 113.45) * mm, "end": v(-2.75, 58.8) * mm, "construction": true});
            skLineSegment(sketch, "E87.MirrorCS", {"start": v(-2.75, -113.45) * mm, "end": v(-2.75, -58.8) * mm, "construction": true});
            skCircle(sketch, "E88.MirrorC", {"center": v(-2.75, -113.45) * mm, "radius": 6 * mm});
            skLineSegment(sketch, "E89.MirrorCS", {"start": v(-16.69, -108) * mm, "end": v(-30.3, -90.3) * mm});
            skLineSegment(sketch, "E90.MirrorCS", {"start": v(11.19, -108) * mm, "end": v(28.9, -90.3) * mm});
            skLineSegment(sketch, "E91.MirrorCS", {"start": v(11.19, -119) * mm, "end": v(11.19, -108) * mm});
            skArc(sketch, "E92.MirrorCS", {"start": v(11.19, -119) * mm, "mid": v(-2.75, -128.45) * mm, "end": v(-16.69, -119) * mm});
            skLineSegment(sketch, "E93.MirrorCS", {"start": v(-16.69, -108) * mm, "end": v(-16.69, -119) * mm});
            skLineSegment(sketch, "E94", {"start": v(-90.47, 0) * mm, "end": v(90.38, 0) * mm, "construction": true});
            skSolve(sketch);
        }
        {
            var Q0;
            Q0=qSketchRegion(id+"F17",true);
            var Q1;
            Q1=qSketchRegion(id+"F16",true);
            var Q2;
            Q2=makeQuery(id+"F2.opExtrude","CAP_FACE",FACE,{"disambiguationData":[OSD([sQuery(id+"F0.wireOp",EDGE,"E12"),sQuery(id+"F0.wireOp",EDGE,"E13"),sQuery(id+"F0.wireOp",EDGE,"E14"),sQuery(id+"F0.wireOp",EDGE,"E15"),sQuery(id+"F0.wireOp",EDGE,"E17.filletArc"),sQuery(id+"F0.wireOp",EDGE,"E18.filletArc"),sQuery(id+"F0.wireOp",EDGE,"E19.filletArc"),sQuery(id+"F0.wireOp",EDGE,"E20.filletArc"),sQuery(id+"F0.wireOp",EDGE,"E25.0"),sQuery(id+"F0.wireOp",EDGE,"E25.1"),sQuery(id+"F0.wireOp",EDGE,"E25.2"),sQuery(id+"F0.wireOp",EDGE,"E25.3"),sQuery(id+"F0.wireOp",EDGE,"E25.4"),sQuery(id+"F0.wireOp",EDGE,"E25.5"),sQuery(id+"F0.wireOp",EDGE,"E25.6"),sQuery(id+"F0.wireOp",EDGE,"E25.7")])],"isStart":false});
            extrude(context, id + "F18", {"entities" : qUnion([Q0, Q1]), "endBound" : BoundingType.UP_TO_SURFACE, "endBoundEntityFace" : qUnion([Q2]), "depth" : 25 * mm});
        }
    });
